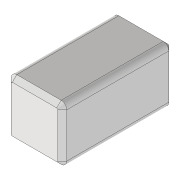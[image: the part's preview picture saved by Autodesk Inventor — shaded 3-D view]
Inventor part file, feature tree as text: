
AUTODESK INVENTOR PART (.ipt)
format: ipt  version: 2020 (Build 240168000, 168)  size: 104,960 bytes
history: native  units: mm
features: extrude x1, chamfer x1, sketch x1
ambient origin geometry x8: Origin, YZ Plane, XZ Plane, XY Plane, X Axis, Y Axis, Z Axis, Center Point
bodies: Volumenkörper1 (feature_tree)
feature tree (3):
  extrude  "Extrusion1"  Depth=100.0mm
  chamfer  "Fase1"  Distance=10.0mm
  sketch  "Skizze1"  dims[d0=100.0mm d1=100.0mm d2=10.0mm d3=200.0mm d4=0.0mm d5=8.0mm d6=2.0mm d7=45.0deg]
